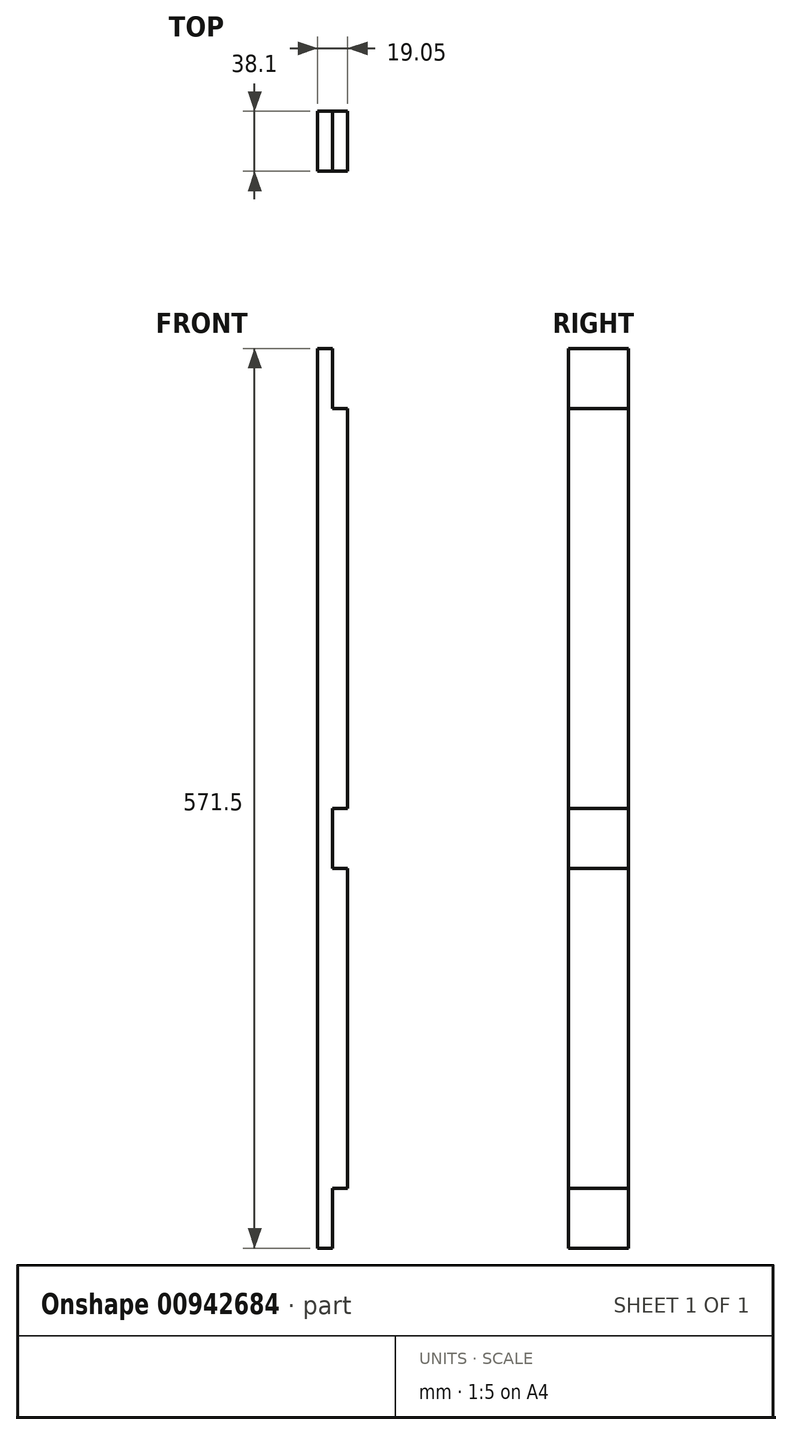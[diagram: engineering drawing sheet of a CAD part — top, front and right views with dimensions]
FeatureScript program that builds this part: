
annotation { "Feature Type Name" : "Feature", "Feature Type Description" : "" }
export const myFeature = defineFeature(function(context is Context, id is Id, definition is map)
    precondition{}
    {
        {
            var Q0;
            Q0=qCreatedBy(makeId("Right.planeOp"),FACE);
            var sketch = newSketch(context, id + "F0", { "sketchPlane" : qUnion([Q0])});
            skLineSegment(sketch, "E0.bottom", {"start": v(19.05, -78.59) * mm, "end": v(-19.05, -78.59) * mm});
            skLineSegment(sketch, "E0.top", {"start": v(19.05, 492.91) * mm, "end": v(-19.05, 492.91) * mm});
            skLineSegment(sketch, "E0.left", {"start": v(19.05, -78.59) * mm, "end": v(19.05, 492.91) * mm});
            skLineSegment(sketch, "E0.right", {"start": v(-19.05, -78.59) * mm, "end": v(-19.05, 492.91) * mm});
            skPoint(sketch, "E0.middle", {"position": v(0, 207.16) * mm});
            skSolve(sketch);
        }
        {
            var Q0;
            Q0=makeQuery(id+"F0.imprint","IMPRINT",FACE,{"disambiguationData":[TD([[makeQuery(id+"F0.imprint","IMPRINT",EDGE,{"derivedFrom":sQuery(id+"F0.wireOp",EDGE,"E0.bottom")}),-1.0]])]});
            extrude(context, id + "F1", {"entities" : qUnion([Q0]), "depth" : 19.05 * mm, "offsetDistance" : 25.4 * mm});
        }
        {
            var Q0;
            Q0=makeQuery(id+"F1.opExtrude","CAP_FACE",FACE,{"disambiguationData":[OSD([sQuery(id+"F0.wireOp",EDGE,"E0.bottom"),sQuery(id+"F0.wireOp",EDGE,"E0.top"),sQuery(id+"F0.wireOp",EDGE,"E0.left"),sQuery(id+"F0.wireOp",EDGE,"E0.right")])],"isStart":false});
            var sketch = newSketch(context, id + "F2", { "sketchPlane" : qUnion([Q0])});
            skLineSegment(sketch, "E1.bottom", {"start": v(-19.05, 492.91) * mm, "end": v(19.05, 492.91) * mm});
            skLineSegment(sketch, "E1.top", {"start": v(-19.05, 454.81) * mm, "end": v(19.05, 454.81) * mm});
            skLineSegment(sketch, "E1.left", {"start": v(-19.05, 492.91) * mm, "end": v(-19.05, 454.81) * mm});
            skLineSegment(sketch, "E1.right", {"start": v(19.05, 492.91) * mm, "end": v(19.05, 454.81) * mm});
            skLineSegment(sketch, "E2.bottom", {"start": v(-19.05, 200.81) * mm, "end": v(19.05, 200.81) * mm});
            skLineSegment(sketch, "E2.top", {"start": v(-19.05, 162.71) * mm, "end": v(19.05, 162.71) * mm});
            skLineSegment(sketch, "E2.left", {"start": v(-19.05, 200.81) * mm, "end": v(-19.05, 162.71) * mm});
            skLineSegment(sketch, "E2.right", {"start": v(19.05, 200.81) * mm, "end": v(19.05, 162.71) * mm});
            skLineSegment(sketch, "E3.bottom", {"start": v(19.05, -78.59) * mm, "end": v(-19.05, -78.59) * mm});
            skLineSegment(sketch, "E3.top", {"start": v(19.05, -40.49) * mm, "end": v(-19.05, -40.49) * mm});
            skLineSegment(sketch, "E3.left", {"start": v(19.05, -78.59) * mm, "end": v(19.05, -40.49) * mm});
            skLineSegment(sketch, "E3.right", {"start": v(-19.05, -78.59) * mm, "end": v(-19.05, -40.49) * mm});
            skSolve(sketch);
        }
        {
            var Q0;
            Q0 = qSketchRegion(id + "F2", true);
            extrude(context, id + "F3", {"entities" : qUnion([Q0]), "operationType" : NewBodyOperationType.REMOVE, "oppositeDirection" : true, "depth" : 9.52 * mm, "offsetDistance" : 25.4 * mm});
        }
    });
